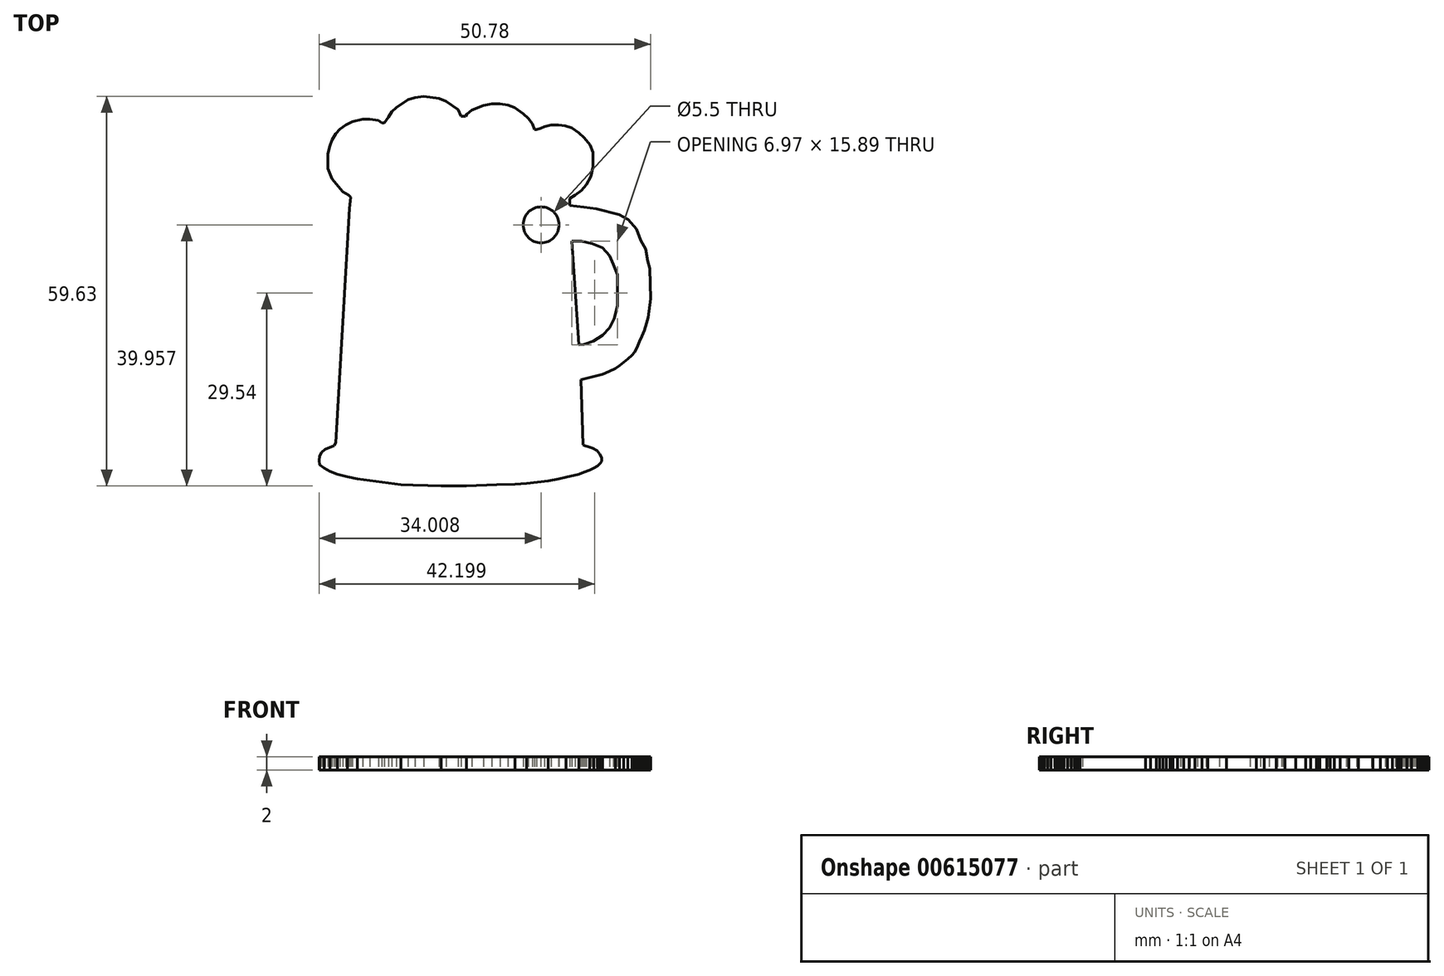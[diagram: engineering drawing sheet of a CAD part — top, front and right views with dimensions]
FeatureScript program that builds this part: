
annotation { "Feature Type Name" : "Feature", "Feature Type Description" : "" }
export const myFeature = defineFeature(function(context is Context, id is Id, definition is map)
    precondition{}
    {
        {
            var Q0;
            Q0=qCreatedBy(makeId("Top.planeOp"),FACE);
            var sketch = newSketch(context, id + "F0", { "sketchPlane" : qUnion([Q0])});
            skLineSegment(sketch, "E0", {"start": v(40.8, 38.36) * mm, "end": v(41.85, 22.48) * mm});
            skLineSegment(sketch, "E1", {"start": v(41.85, 22.48) * mm, "end": v(42.62, 22.53) * mm});
            skLineSegment(sketch, "E2", {"start": v(42.62, 22.53) * mm, "end": v(44.12, 23.04) * mm});
            skLineSegment(sketch, "E3", {"start": v(44.12, 23.04) * mm, "end": v(45.5, 23.94) * mm});
            skLineSegment(sketch, "E4", {"start": v(45.5, 23.94) * mm, "end": v(46.55, 25.07) * mm});
            skLineSegment(sketch, "E5", {"start": v(46.55, 25.07) * mm, "end": v(47.28, 26.45) * mm});
            skLineSegment(sketch, "E6", {"start": v(47.28, 26.45) * mm, "end": v(47.76, 28.43) * mm});
            skLineSegment(sketch, "E7", {"start": v(47.76, 28.43) * mm, "end": v(47.76, 31.4) * mm});
            skLineSegment(sketch, "E8", {"start": v(47.76, 31.4) * mm, "end": v(47.76, 33.18) * mm});
            skLineSegment(sketch, "E9", {"start": v(47.76, 33.18) * mm, "end": v(47.12, 34.76) * mm});
            skLineSegment(sketch, "E10", {"start": v(47.12, 34.76) * mm, "end": v(46.55, 36.1) * mm});
            skLineSegment(sketch, "E11", {"start": v(46.55, 36.1) * mm, "end": v(45.5, 37.3) * mm});
            skLineSegment(sketch, "E12", {"start": v(45.5, 37.3) * mm, "end": v(43.87, 37.96) * mm});
            skLineSegment(sketch, "E13", {"start": v(43.87, 37.96) * mm, "end": v(42.25, 38.32) * mm});
            skLineSegment(sketch, "E14", {"start": v(42.25, 38.32) * mm, "end": v(40.8, 38.36) * mm});
            skLineSegment(sketch, "E15", {"start": v(40.47, 43.8) * mm, "end": v(40.47, 44.9) * mm});
            skLineSegment(sketch, "E16", {"start": v(40.47, 44.9) * mm, "end": v(41.29, 45.38) * mm});
            skLineSegment(sketch, "E17", {"start": v(41.29, 45.38) * mm, "end": v(42.24, 46.06) * mm});
            skLineSegment(sketch, "E18", {"start": v(42.24, 46.06) * mm, "end": v(43, 46.95) * mm});
            skLineSegment(sketch, "E19", {"start": v(43, 46.95) * mm, "end": v(43.68, 48.27) * mm});
            skLineSegment(sketch, "E20", {"start": v(43.68, 48.27) * mm, "end": v(44.02, 49.73) * mm});
            skLineSegment(sketch, "E21", {"start": v(44.02, 49.73) * mm, "end": v(44.02, 50.65) * mm});
            skLineSegment(sketch, "E22", {"start": v(44.02, 50.65) * mm, "end": v(44.02, 51.94) * mm});
            skLineSegment(sketch, "E23", {"start": v(44.02, 51.94) * mm, "end": v(43.58, 53.08) * mm});
            skLineSegment(sketch, "E24", {"start": v(43.58, 53.08) * mm, "end": v(42.7, 54.16) * mm});
            skLineSegment(sketch, "E25", {"start": v(42.7, 54.16) * mm, "end": v(41.85, 54.9) * mm});
            skLineSegment(sketch, "E26", {"start": v(41.85, 54.9) * mm, "end": v(40.8, 55.66) * mm});
            skLineSegment(sketch, "E27", {"start": v(40.8, 55.66) * mm, "end": v(39.76, 55.96) * mm});
            skLineSegment(sketch, "E28", {"start": v(39.76, 55.96) * mm, "end": v(38.74, 56.1) * mm});
            skLineSegment(sketch, "E29", {"start": v(38.74, 56.1) * mm, "end": v(37.58, 56.1) * mm});
            skLineSegment(sketch, "E30", {"start": v(37.58, 56.1) * mm, "end": v(36.63, 55.88) * mm});
            skLineSegment(sketch, "E31", {"start": v(36.63, 55.88) * mm, "end": v(36.01, 55.62) * mm});
            skLineSegment(sketch, "E32", {"start": v(36.01, 55.62) * mm, "end": v(35.4, 55.4) * mm});
            skLineSegment(sketch, "E33", {"start": v(35.4, 55.4) * mm, "end": v(35.1, 55.4) * mm});
            skLineSegment(sketch, "E34", {"start": v(35.1, 55.4) * mm, "end": v(34.73, 56.3) * mm});
            skLineSegment(sketch, "E35", {"start": v(34.73, 56.3) * mm, "end": v(34.12, 57.16) * mm});
            skLineSegment(sketch, "E36", {"start": v(34.12, 57.16) * mm, "end": v(33.36, 57.84) * mm});
            skLineSegment(sketch, "E37", {"start": v(33.36, 57.84) * mm, "end": v(32.04, 58.78) * mm});
            skLineSegment(sketch, "E38", {"start": v(32.04, 58.78) * mm, "end": v(31.03, 59.17) * mm});
            skLineSegment(sketch, "E39", {"start": v(31.03, 59.17) * mm, "end": v(29.8, 59.33) * mm});
            skLineSegment(sketch, "E40", {"start": v(29.8, 59.33) * mm, "end": v(28.54, 59.33) * mm});
            skLineSegment(sketch, "E41", {"start": v(28.54, 59.33) * mm, "end": v(27.28, 59.13) * mm});
            skLineSegment(sketch, "E42", {"start": v(27.28, 59.13) * mm, "end": v(26.35, 58.74) * mm});
            skLineSegment(sketch, "E43", {"start": v(26.35, 58.74) * mm, "end": v(25.5, 58.4) * mm});
            skLineSegment(sketch, "E44", {"start": v(25.5, 58.4) * mm, "end": v(24.73, 57.75) * mm});
            skLineSegment(sketch, "E45", {"start": v(24.73, 57.75) * mm, "end": v(24.5, 57.44) * mm});
            skLineSegment(sketch, "E46", {"start": v(24.5, 57.44) * mm, "end": v(23.8, 57.44) * mm});
            skLineSegment(sketch, "E47", {"start": v(23.8, 57.44) * mm, "end": v(23.38, 58.45) * mm});
            skLineSegment(sketch, "E48", {"start": v(23.38, 58.45) * mm, "end": v(22.43, 59.13) * mm});
            skLineSegment(sketch, "E49", {"start": v(22.43, 59.13) * mm, "end": v(21.57, 59.75) * mm});
            skLineSegment(sketch, "E50", {"start": v(21.57, 59.75) * mm, "end": v(20.46, 60.2) * mm});
            skLineSegment(sketch, "E51", {"start": v(20.46, 60.2) * mm, "end": v(19.3, 60.35) * mm});
            skLineSegment(sketch, "E52", {"start": v(19.3, 60.35) * mm, "end": v(18.1, 60.5) * mm});
            skLineSegment(sketch, "E53", {"start": v(18.1, 60.5) * mm, "end": v(16.78, 60.3) * mm});
            skLineSegment(sketch, "E54", {"start": v(16.78, 60.3) * mm, "end": v(15.68, 60) * mm});
            skLineSegment(sketch, "E55", {"start": v(15.68, 60) * mm, "end": v(14.73, 59.33) * mm});
            skLineSegment(sketch, "E56", {"start": v(14.73, 59.33) * mm, "end": v(13.94, 58.79) * mm});
            skLineSegment(sketch, "E57", {"start": v(13.94, 58.79) * mm, "end": v(13.21, 58.18) * mm});
            skLineSegment(sketch, "E58", {"start": v(13.21, 58.18) * mm, "end": v(12.72, 57.32) * mm});
            skLineSegment(sketch, "E59", {"start": v(12.72, 57.32) * mm, "end": v(12.37, 56.83) * mm});
            skLineSegment(sketch, "E60", {"start": v(12.37, 56.83) * mm, "end": v(12.1, 56.45) * mm});
            skLineSegment(sketch, "E61", {"start": v(12.1, 56.45) * mm, "end": v(11.7, 56.45) * mm});
            skLineSegment(sketch, "E62", {"start": v(11.7, 56.45) * mm, "end": v(11.18, 56.83) * mm});
            skLineSegment(sketch, "E63", {"start": v(11.18, 56.83) * mm, "end": v(9.89, 57) * mm});
            skLineSegment(sketch, "E64", {"start": v(9.89, 57) * mm, "end": v(8.77, 57) * mm});
            skLineSegment(sketch, "E65", {"start": v(8.77, 57) * mm, "end": v(7.2, 56.63) * mm});
            skLineSegment(sketch, "E66", {"start": v(7.2, 56.63) * mm, "end": v(6.2, 56.1) * mm});
            skLineSegment(sketch, "E67", {"start": v(6.2, 56.1) * mm, "end": v(5.29, 55.47) * mm});
            skLineSegment(sketch, "E68", {"start": v(5.29, 55.47) * mm, "end": v(4.67, 54.78) * mm});
            skLineSegment(sketch, "E69", {"start": v(4.67, 54.78) * mm, "end": v(4.1, 53.84) * mm});
            skLineSegment(sketch, "E70", {"start": v(4.1, 53.84) * mm, "end": v(3.75, 52.94) * mm});
            skLineSegment(sketch, "E71", {"start": v(3.75, 52.94) * mm, "end": v(3.44, 51.73) * mm});
            skLineSegment(sketch, "E72", {"start": v(3.44, 51.73) * mm, "end": v(3.44, 50.83) * mm});
            skLineSegment(sketch, "E73", {"start": v(3.44, 50.83) * mm, "end": v(3.44, 49.46) * mm});
            skLineSegment(sketch, "E74", {"start": v(3.44, 49.46) * mm, "end": v(3.75, 48.71) * mm});
            skLineSegment(sketch, "E75", {"start": v(3.75, 48.71) * mm, "end": v(4.1, 47.86) * mm});
            skLineSegment(sketch, "E76", {"start": v(4.1, 47.86) * mm, "end": v(4.87, 46.93) * mm});
            skLineSegment(sketch, "E77", {"start": v(4.87, 46.93) * mm, "end": v(5.71, 45.9) * mm});
            skLineSegment(sketch, "E78", {"start": v(5.71, 45.9) * mm, "end": v(6.59, 45.38) * mm});
            skLineSegment(sketch, "E79", {"start": v(6.59, 45.38) * mm, "end": v(6.96, 45.05) * mm});
            skLineSegment(sketch, "E80", {"start": v(6.96, 45.05) * mm, "end": v(6.73, 43.35) * mm});
            skLineSegment(sketch, "E81", {"start": v(6.73, 43.35) * mm, "end": v(4.67, 7.5) * mm});
            skLineSegment(sketch, "E82", {"start": v(4.67, 7.5) * mm, "end": v(4.38, 7) * mm});
            skLineSegment(sketch, "E83", {"start": v(4.38, 7) * mm, "end": v(3.75, 6.74) * mm});
            skLineSegment(sketch, "E84", {"start": v(3.75, 6.74) * mm, "end": v(3.02, 6.44) * mm});
            skLineSegment(sketch, "E85", {"start": v(3.02, 6.44) * mm, "end": v(2.51, 6.02) * mm});
            skLineSegment(sketch, "E86", {"start": v(2.51, 6.02) * mm, "end": v(2.18, 5.47) * mm});
            skLineSegment(sketch, "E87", {"start": v(2.18, 5.47) * mm, "end": v(2.08, 4.75) * mm});
            skLineSegment(sketch, "E88", {"start": v(2.08, 4.75) * mm, "end": v(2.19, 4.12) * mm});
            skLineSegment(sketch, "E89", {"start": v(2.19, 4.12) * mm, "end": v(2.86, 3.63) * mm});
            skLineSegment(sketch, "E90", {"start": v(2.86, 3.63) * mm, "end": v(3.75, 3.1) * mm});
            skLineSegment(sketch, "E91", {"start": v(3.75, 3.1) * mm, "end": v(4.91, 2.63) * mm});
            skLineSegment(sketch, "E92", {"start": v(4.91, 2.63) * mm, "end": v(6.41, 2.27) * mm});
            skLineSegment(sketch, "E93", {"start": v(6.41, 2.27) * mm, "end": v(7.98, 1.93) * mm});
            skLineSegment(sketch, "E94", {"start": v(7.98, 1.93) * mm, "end": v(9.45, 1.74) * mm});
            skLineSegment(sketch, "E95", {"start": v(9.45, 1.74) * mm, "end": v(10.98, 1.53) * mm});
            skLineSegment(sketch, "E96", {"start": v(10.98, 1.53) * mm, "end": v(12.7, 1.3) * mm});
            skLineSegment(sketch, "E97", {"start": v(12.7, 1.3) * mm, "end": v(14.64, 1.05) * mm});
            skLineSegment(sketch, "E98", {"start": v(14.64, 1.05) * mm, "end": v(16.43, 1) * mm});
            skLineSegment(sketch, "E99", {"start": v(16.43, 1) * mm, "end": v(18.76, 0.93) * mm});
            skLineSegment(sketch, "E100", {"start": v(18.76, 0.93) * mm, "end": v(20.76, 0.88) * mm});
            skLineSegment(sketch, "E101", {"start": v(20.76, 0.88) * mm, "end": v(24.67, 0.88) * mm});
            skLineSegment(sketch, "E102", {"start": v(24.67, 0.88) * mm, "end": v(29.28, 1.05) * mm});
            skLineSegment(sketch, "E103", {"start": v(29.28, 1.05) * mm, "end": v(32.08, 1.13) * mm});
            skLineSegment(sketch, "E104", {"start": v(32.08, 1.13) * mm, "end": v(33.87, 1.22) * mm});
            skLineSegment(sketch, "E105", {"start": v(33.87, 1.22) * mm, "end": v(35.48, 1.43) * mm});
            skLineSegment(sketch, "E106", {"start": v(35.48, 1.43) * mm, "end": v(37.14, 1.64) * mm});
            skLineSegment(sketch, "E107", {"start": v(37.14, 1.64) * mm, "end": v(38.82, 1.96) * mm});
            skLineSegment(sketch, "E108", {"start": v(38.82, 1.96) * mm, "end": v(39.92, 2.18) * mm});
            skLineSegment(sketch, "E109", {"start": v(39.92, 2.18) * mm, "end": v(41.02, 2.45) * mm});
            skLineSegment(sketch, "E110", {"start": v(41.02, 2.45) * mm, "end": v(41.86, 2.66) * mm});
            skLineSegment(sketch, "E111", {"start": v(41.86, 2.66) * mm, "end": v(42.64, 2.95) * mm});
            skLineSegment(sketch, "E112", {"start": v(42.64, 2.95) * mm, "end": v(43.52, 3.28) * mm});
            skLineSegment(sketch, "E113", {"start": v(43.52, 3.28) * mm, "end": v(44.18, 3.63) * mm});
            skLineSegment(sketch, "E114", {"start": v(44.18, 3.63) * mm, "end": v(44.73, 3.95) * mm});
            skLineSegment(sketch, "E115", {"start": v(44.73, 3.95) * mm, "end": v(45.13, 4.3) * mm});
            skLineSegment(sketch, "E116", {"start": v(45.13, 4.3) * mm, "end": v(45.34, 4.65) * mm});
            skLineSegment(sketch, "E117", {"start": v(45.34, 4.65) * mm, "end": v(45.32, 5.2) * mm});
            skLineSegment(sketch, "E118", {"start": v(45.32, 5.2) * mm, "end": v(45.05, 5.77) * mm});
            skLineSegment(sketch, "E119", {"start": v(45.05, 5.77) * mm, "end": v(44.64, 6.26) * mm});
            skLineSegment(sketch, "E120", {"start": v(44.64, 6.26) * mm, "end": v(43.96, 6.64) * mm});
            skLineSegment(sketch, "E121", {"start": v(43.96, 6.64) * mm, "end": v(43.4, 6.81) * mm});
            skLineSegment(sketch, "E122", {"start": v(43.4, 6.81) * mm, "end": v(42.72, 7.03) * mm});
            skLineSegment(sketch, "E123", {"start": v(42.72, 7.03) * mm, "end": v(42.52, 7.13) * mm});
            skLineSegment(sketch, "E124", {"start": v(42.52, 7.13) * mm, "end": v(42.16, 17.12) * mm});
            skLineSegment(sketch, "E125", {"start": v(42.16, 17.12) * mm, "end": v(43.05, 17.34) * mm});
            skLineSegment(sketch, "E126", {"start": v(43.05, 17.34) * mm, "end": v(44.28, 17.65) * mm});
            skLineSegment(sketch, "E127", {"start": v(44.28, 17.65) * mm, "end": v(45.45, 17.94) * mm});
            skLineSegment(sketch, "E128", {"start": v(45.45, 17.94) * mm, "end": v(46.49, 18.39) * mm});
            skLineSegment(sketch, "E129", {"start": v(46.49, 18.39) * mm, "end": v(47.48, 18.82) * mm});
            skLineSegment(sketch, "E130", {"start": v(47.48, 18.82) * mm, "end": v(48.07, 19.27) * mm});
            skLineSegment(sketch, "E131", {"start": v(48.07, 19.27) * mm, "end": v(48.75, 19.82) * mm});
            skLineSegment(sketch, "E132", {"start": v(48.75, 19.82) * mm, "end": v(49.34, 20.31) * mm});
            skLineSegment(sketch, "E133", {"start": v(49.34, 20.31) * mm, "end": v(49.96, 20.9) * mm});
            skLineSegment(sketch, "E134", {"start": v(49.96, 20.9) * mm, "end": v(50.38, 21.32) * mm});
            skLineSegment(sketch, "E135", {"start": v(50.38, 21.32) * mm, "end": v(50.73, 22.04) * mm});
            skLineSegment(sketch, "E136", {"start": v(50.73, 22.04) * mm, "end": v(51.14, 23) * mm});
            skLineSegment(sketch, "E137", {"start": v(51.14, 23) * mm, "end": v(51.51, 23.8) * mm});
            skLineSegment(sketch, "E138", {"start": v(51.51, 23.8) * mm, "end": v(51.86, 24.67) * mm});
            skLineSegment(sketch, "E139", {"start": v(51.86, 24.67) * mm, "end": v(52.24, 25.78) * mm});
            skLineSegment(sketch, "E140", {"start": v(52.24, 25.78) * mm, "end": v(52.48, 26.68) * mm});
            skLineSegment(sketch, "E141", {"start": v(52.48, 26.68) * mm, "end": v(52.66, 28) * mm});
            skLineSegment(sketch, "E142", {"start": v(52.66, 28) * mm, "end": v(52.86, 29.5) * mm});
            skLineSegment(sketch, "E143", {"start": v(52.86, 29.5) * mm, "end": v(52.7, 34.13) * mm});
            skLineSegment(sketch, "E144", {"start": v(52.7, 34.13) * mm, "end": v(52.4, 35.3) * mm});
            skLineSegment(sketch, "E145", {"start": v(52.4, 35.3) * mm, "end": v(52.06, 37.14) * mm});
            skLineSegment(sketch, "E146", {"start": v(52.06, 37.14) * mm, "end": v(51.34, 38.46) * mm});
            skLineSegment(sketch, "E147", {"start": v(51.34, 38.46) * mm, "end": v(50.7, 40.15) * mm});
            skLineSegment(sketch, "E148", {"start": v(50.7, 40.15) * mm, "end": v(49.44, 41.67) * mm});
            skLineSegment(sketch, "E149", {"start": v(49.44, 41.67) * mm, "end": v(48, 42.39) * mm});
            skLineSegment(sketch, "E150", {"start": v(48, 42.39) * mm, "end": v(46.35, 42.83) * mm});
            skLineSegment(sketch, "E151", {"start": v(46.35, 42.83) * mm, "end": v(44.52, 43.32) * mm});
            skLineSegment(sketch, "E152", {"start": v(44.52, 43.32) * mm, "end": v(42.61, 43.58) * mm});
            skLineSegment(sketch, "E153", {"start": v(42.61, 43.58) * mm, "end": v(40.47, 43.8) * mm});
            skCircle(sketch, "E154", {"center": v(36.09, 40.84) * mm, "radius": 2.75 * mm});
            skLineSegment(sketch, "E155", {"start": v(20.13, 45.87) * mm, "end": v(20.22, 46.24) * mm});
            skLineSegment(sketch, "E156", {"start": v(20.22, 46.24) * mm, "end": v(20.52, 46.5) * mm});
            skLineSegment(sketch, "E157", {"start": v(20.52, 46.5) * mm, "end": v(21.08, 46.51) * mm});
            skLineSegment(sketch, "E158", {"start": v(21.08, 46.51) * mm, "end": v(39.3, 46.8) * mm});
            skLineSegment(sketch, "E159", {"start": v(39.3, 46.8) * mm, "end": v(39.83, 47.12) * mm});
            skLineSegment(sketch, "E160", {"start": v(39.83, 47.12) * mm, "end": v(40.34, 47.48) * mm});
            skLineSegment(sketch, "E161", {"start": v(40.34, 47.48) * mm, "end": v(41.26, 48.27) * mm});
            skLineSegment(sketch, "E162", {"start": v(41.26, 48.27) * mm, "end": v(41.64, 48.96) * mm});
            skLineSegment(sketch, "E163", {"start": v(41.64, 48.96) * mm, "end": v(42.02, 50) * mm});
            skLineSegment(sketch, "E164", {"start": v(42.02, 50) * mm, "end": v(42, 51) * mm});
            skLineSegment(sketch, "E165", {"start": v(42, 51) * mm, "end": v(41.64, 51.82) * mm});
            skLineSegment(sketch, "E166", {"start": v(41.64, 51.82) * mm, "end": v(40.78, 52.82) * mm});
            skLineSegment(sketch, "E167", {"start": v(40.78, 52.82) * mm, "end": v(39.68, 53.42) * mm});
            skLineSegment(sketch, "E168", {"start": v(39.68, 53.42) * mm, "end": v(38.45, 53.74) * mm});
            skLineSegment(sketch, "E169", {"start": v(38.45, 53.74) * mm, "end": v(37.35, 53.72) * mm});
            skLineSegment(sketch, "E170", {"start": v(37.35, 53.72) * mm, "end": v(36.7, 53.5) * mm});
            skLineSegment(sketch, "E171", {"start": v(36.7, 53.5) * mm, "end": v(36, 52.9) * mm});
            skLineSegment(sketch, "E172", {"start": v(36, 52.9) * mm, "end": v(35.49, 52.46) * mm});
            skLineSegment(sketch, "E173", {"start": v(35.49, 52.46) * mm, "end": v(35.12, 52.15) * mm});
            skLineSegment(sketch, "E174", {"start": v(35.12, 52.15) * mm, "end": v(34.47, 52.24) * mm});
            skLineSegment(sketch, "E175", {"start": v(34.47, 52.24) * mm, "end": v(33.85, 52.5) * mm});
            skLineSegment(sketch, "E176", {"start": v(33.85, 52.5) * mm, "end": v(33.54, 53.06) * mm});
            skLineSegment(sketch, "E177", {"start": v(33.54, 53.06) * mm, "end": v(33.54, 54) * mm});
            skLineSegment(sketch, "E178", {"start": v(33.54, 54) * mm, "end": v(33.24, 54.68) * mm});
            skLineSegment(sketch, "E179", {"start": v(33.24, 54.68) * mm, "end": v(32.86, 55.4) * mm});
            skLineSegment(sketch, "E180", {"start": v(32.86, 55.4) * mm, "end": v(32.35, 55.99) * mm});
            skLineSegment(sketch, "E181", {"start": v(32.35, 55.99) * mm, "end": v(31.72, 56.48) * mm});
            skLineSegment(sketch, "E182", {"start": v(31.72, 56.48) * mm, "end": v(30.92, 56.91) * mm});
            skLineSegment(sketch, "E183", {"start": v(30.92, 56.91) * mm, "end": v(30.23, 57.16) * mm});
            skLineSegment(sketch, "E184", {"start": v(30.23, 57.16) * mm, "end": v(29.38, 57.26) * mm});
            skLineSegment(sketch, "E185", {"start": v(29.38, 57.26) * mm, "end": v(28.55, 57.16) * mm});
            skLineSegment(sketch, "E186", {"start": v(28.55, 57.16) * mm, "end": v(27.65, 57) * mm});
            skLineSegment(sketch, "E187", {"start": v(27.65, 57) * mm, "end": v(27.1, 56.69) * mm});
            skLineSegment(sketch, "E188", {"start": v(27.1, 56.69) * mm, "end": v(26.42, 56.1) * mm});
            skLineSegment(sketch, "E189", {"start": v(26.42, 56.1) * mm, "end": v(25.8, 55.57) * mm});
            skLineSegment(sketch, "E190", {"start": v(25.8, 55.57) * mm, "end": v(25.4, 55) * mm});
            skLineSegment(sketch, "E191", {"start": v(25.4, 55) * mm, "end": v(25.18, 54.6) * mm});
            skLineSegment(sketch, "E192", {"start": v(25.18, 54.6) * mm, "end": v(24.91, 54.11) * mm});
            skLineSegment(sketch, "E193", {"start": v(24.91, 54.11) * mm, "end": v(24.7, 53.92) * mm});
            skLineSegment(sketch, "E194", {"start": v(24.7, 53.92) * mm, "end": v(24.35, 53.86) * mm});
            skLineSegment(sketch, "E195", {"start": v(24.35, 53.86) * mm, "end": v(23.43, 53.84) * mm});
            skLineSegment(sketch, "E196", {"start": v(23.43, 53.84) * mm, "end": v(23.06, 54.27) * mm});
            skLineSegment(sketch, "E197", {"start": v(23.06, 54.27) * mm, "end": v(22.94, 54.96) * mm});
            skLineSegment(sketch, "E198", {"start": v(22.94, 54.96) * mm, "end": v(22.75, 55.64) * mm});
            skLineSegment(sketch, "E199", {"start": v(22.75, 55.64) * mm, "end": v(22.35, 56.27) * mm});
            skLineSegment(sketch, "E200", {"start": v(22.35, 56.27) * mm, "end": v(21.9, 57) * mm});
            skLineSegment(sketch, "E201", {"start": v(21.9, 57) * mm, "end": v(21.3, 57.54) * mm});
            skLineSegment(sketch, "E202", {"start": v(21.3, 57.54) * mm, "end": v(20.68, 57.88) * mm});
            skLineSegment(sketch, "E203", {"start": v(20.68, 57.88) * mm, "end": v(19.87, 58.32) * mm});
            skLineSegment(sketch, "E204", {"start": v(19.87, 58.32) * mm, "end": v(18.87, 58.3) * mm});
            skLineSegment(sketch, "E205", {"start": v(18.87, 58.3) * mm, "end": v(17.42, 58.28) * mm});
            skLineSegment(sketch, "E206", {"start": v(17.42, 58.28) * mm, "end": v(16.49, 58.03) * mm});
            skLineSegment(sketch, "E207", {"start": v(16.49, 58.03) * mm, "end": v(15.85, 57.58) * mm});
            skLineSegment(sketch, "E208", {"start": v(15.85, 57.58) * mm, "end": v(15.28, 57.08) * mm});
            skLineSegment(sketch, "E209", {"start": v(15.28, 57.08) * mm, "end": v(14.74, 56.61) * mm});
            skLineSegment(sketch, "E210", {"start": v(14.74, 56.61) * mm, "end": v(14.18, 55.88) * mm});
            skLineSegment(sketch, "E211", {"start": v(14.18, 55.88) * mm, "end": v(13.93, 55.26) * mm});
            skLineSegment(sketch, "E212", {"start": v(13.93, 55.26) * mm, "end": v(13.73, 54.5) * mm});
            skLineSegment(sketch, "E213", {"start": v(13.73, 54.5) * mm, "end": v(13.48, 54.05) * mm});
            skSolve(sketch);
        }
        {
            var Q0;
            Q0=makeQuery(id+"F0.imprint","IMPRINT",FACE,{"disambiguationData":[TD([[makeQuery(id+"F0.imprint","IMPRINT",EDGE,{"derivedFrom":sQuery(id+"F0.wireOp",EDGE,"E0")}),-1.0]])]});
            extrude(context, id + "F1", {"entities" : qUnion([Q0]), "depth" : 2 * mm, "offsetDistance" : 25 * mm});
        }
    });
